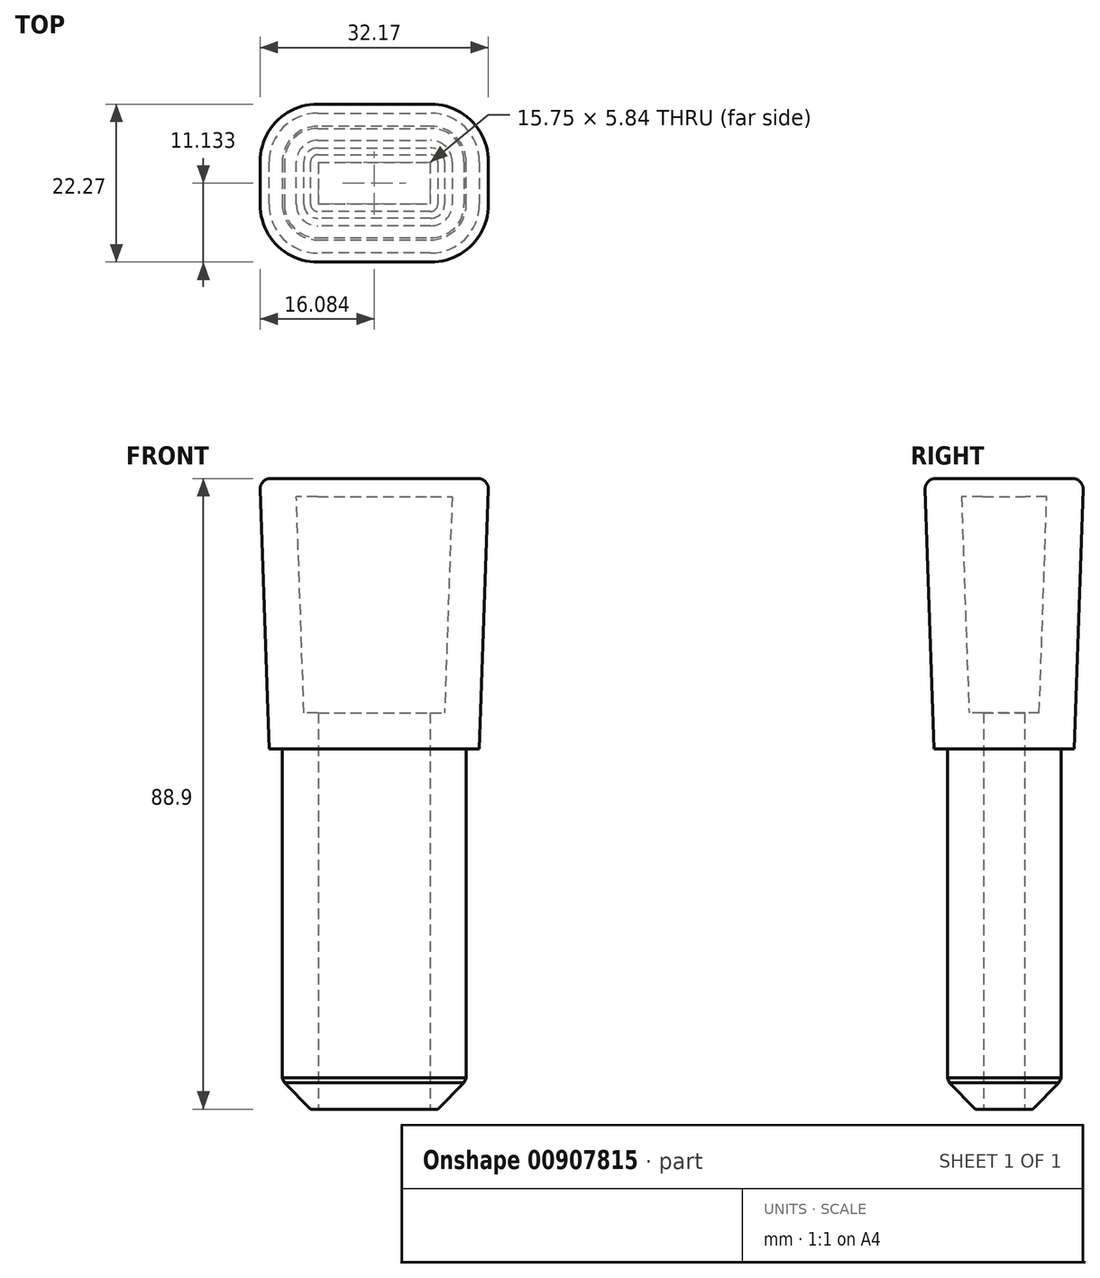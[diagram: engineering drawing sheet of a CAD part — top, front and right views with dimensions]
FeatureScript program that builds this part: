
annotation { "Feature Type Name" : "Feature", "Feature Type Description" : "" }
export const myFeature = defineFeature(function(context is Context, id is Id, definition is map)
    precondition{}
    {
        {
            var Q0;
            Q0=qCreatedBy(makeId("Top.planeOp"),FACE);
            var sketch = newSketch(context, id + "F0", { "sketchPlane" : qUnion([Q0])});
            skLineSegment(sketch, "E0.bottom", {"start": v(5, 0.5) * mm, "end": v(20.9, 0.5) * mm});
            skLineSegment(sketch, "E0.top", {"start": v(5, -15.5) * mm, "end": v(20.9, -15.5) * mm});
            skLineSegment(sketch, "E0.left", {"start": v(0, -4.5) * mm, "end": v(0, -10.5) * mm});
            skLineSegment(sketch, "E0.right", {"start": v(25.9, -4.5) * mm, "end": v(25.9, -10.5) * mm});
            skPoint(sketch, "E1.visualSharp", {"position": v(0, 0.5) * mm});
            skArc(sketch, "E1.filletArc", {"start": v(5, 0.5) * mm, "mid": v(1.46, -0.97) * mm, "end": v(0, -4.5) * mm});
            skPoint(sketch, "E2.visualSharp", {"position": v(25.9, 0.5) * mm});
            skArc(sketch, "E2.filletArc", {"start": v(25.9, -4.5) * mm, "mid": v(24.44, -0.97) * mm, "end": v(20.9, 0.5) * mm});
            skPoint(sketch, "E3.visualSharp", {"position": v(25.9, -15.5) * mm});
            skArc(sketch, "E3.filletArc", {"start": v(20.9, -15.5) * mm, "mid": v(24.44, -14.04) * mm, "end": v(25.9, -10.5) * mm});
            skPoint(sketch, "E4.visualSharp", {"position": v(0, -15.5) * mm});
            skArc(sketch, "E4.filletArc", {"start": v(0, -10.5) * mm, "mid": v(1.46, -14.04) * mm, "end": v(5, -15.5) * mm});
            skSolve(sketch);
        }
        {
            var Q0;
            Q0=makeQuery(id+"F0.imprint","IMPRINT",FACE,{"disambiguationData":[TD([[makeQuery(id+"F0.imprint","IMPRINT",EDGE,{"derivedFrom":sQuery(id+"F0.wireOp",EDGE,"E0.bottom")}),-1.0]])]});
            extrude(context, id + "F1", {"entities" : qUnion([Q0]), "depth" : 50.8 * mm, "offsetDistance" : 25 * mm});
        }
        {
            var Q0;
            Q0=makeQuery(id+"F1.opExtrude","CAP_FACE",FACE,{"disambiguationData":[OSD([sQuery(id+"F0.wireOp",EDGE,"E0.bottom"),sQuery(id+"F0.wireOp",EDGE,"E0.top"),sQuery(id+"F0.wireOp",EDGE,"E0.left"),sQuery(id+"F0.wireOp",EDGE,"E0.right"),sQuery(id+"F0.wireOp",EDGE,"E1.filletArc"),sQuery(id+"F0.wireOp",EDGE,"E2.filletArc"),sQuery(id+"F0.wireOp",EDGE,"E3.filletArc"),sQuery(id+"F0.wireOp",EDGE,"E4.filletArc")])],"isStart":false});
            var sketch = newSketch(context, id + "F2", { "sketchPlane" : qUnion([Q0])});
            skArc(sketch, "E5.0", {"start": v(5, 2.35) * mm, "mid": v(0.15, 0.34) * mm, "end": v(-1.85, -4.5) * mm});
            skLineSegment(sketch, "E5.1", {"start": v(-1.85, -4.5) * mm, "end": v(-1.85, -10.5) * mm});
            skLineSegment(sketch, "E5.2", {"start": v(5, 2.35) * mm, "end": v(20.9, 2.35) * mm});
            skArc(sketch, "E5.3", {"start": v(-1.85, -10.5) * mm, "mid": v(0.15, -15.35) * mm, "end": v(5, -17.36) * mm});
            skArc(sketch, "E5.4", {"start": v(27.76, -4.5) * mm, "mid": v(25.75, 0.34) * mm, "end": v(20.9, 2.35) * mm});
            skLineSegment(sketch, "E5.5", {"start": v(27.76, -4.5) * mm, "end": v(27.76, -10.5) * mm});
            skArc(sketch, "E5.6", {"start": v(20.9, -17.36) * mm, "mid": v(25.75, -15.35) * mm, "end": v(27.76, -10.5) * mm});
            skLineSegment(sketch, "E5.7", {"start": v(5, -17.36) * mm, "end": v(20.9, -17.36) * mm});
            skSolve(sketch);
        }
        {
            var Q0;
            Q0 = qSketchRegion(id + "F2", true);
            extrude(context, id + "F3", {"entities" : qUnion([Q0]), "operationType" : NewBodyOperationType.ADD, "depth" : 38.1 * mm, "offsetDistance" : 25 * mm, "hasDraft" : true, "draftAngle" : 2 * degree});
        }
        {
            var Q0;
            Q0=makeQuery(id+"F3.opExtrude","CAP_FACE",FACE,{"disambiguationData":[OSD([sQuery(id+"F2.wireOp",EDGE,"E5.0"),sQuery(id+"F2.wireOp",EDGE,"E5.1"),sQuery(id+"F2.wireOp",EDGE,"E5.2"),sQuery(id+"F2.wireOp",EDGE,"E5.3"),sQuery(id+"F2.wireOp",EDGE,"E5.4"),sQuery(id+"F2.wireOp",EDGE,"E5.5"),sQuery(id+"F2.wireOp",EDGE,"E5.6"),sQuery(id+"F2.wireOp",EDGE,"E5.7")])],"isStart":false});
            var Q1;
            Q1=makeQuery(id+"F1.opExtrude","CAP_FACE",FACE,{"disambiguationData":[OSD([sQuery(id+"F0.wireOp",EDGE,"E0.bottom"),sQuery(id+"F0.wireOp",EDGE,"E0.top"),sQuery(id+"F0.wireOp",EDGE,"E0.left"),sQuery(id+"F0.wireOp",EDGE,"E0.right"),sQuery(id+"F0.wireOp",EDGE,"E1.filletArc"),sQuery(id+"F0.wireOp",EDGE,"E2.filletArc"),sQuery(id+"F0.wireOp",EDGE,"E3.filletArc"),sQuery(id+"F0.wireOp",EDGE,"E4.filletArc")])],"isStart":true});
            shell(context, id + "F4", {"entities" : qUnion([Q0, Q1]), "thickness" : 5.08 * mm});
        }
        {
            var Q0;
            Q0=makeQuery(id+"F1.opExtrude","CAP_EDGE",EDGE,{"disambiguationData":[OSD([sQuery(id+"F0.wireOp",EDGE,"E0.top")])],"isStart":true});
            chamfer(context, id + "F5", {"entities" : qUnion([Q0]), "width" : 4 * mm, "tangentPropagation" : true});
        }
        {
            var Q0;
            {var subQ0=sQuery(id+"F0.wireOp",EDGE,"E0.left");Q0=makeQuery(id+"F5.opChamfer","BLEND_EDGE",EDGE,{"blendedFrom":[makeQuery(id+"F1.opExtrude","CAP_EDGE",EDGE,{"disambiguationData":[OSD([subQ0])],"isStart":true}),makeQuery(id+"F1.opExtrude","SWEPT_FACE",FACE,{"disambiguationData":[OSD([subQ0])]})],"blendedInto":[makeQuery(id+"F1.opExtrude","SWEPT_FACE",FACE,{"disambiguationData":[OSD([subQ0])]})]});}
            chamfer(context, id + "F6", {"entities" : qUnion([Q0]), "width" : 1 * mm, "tangentPropagation" : true});
        }
        {
            var Q0;
            Q0=makeQuery(id+"F3.opExtrude","CAP_FACE",FACE,{"disambiguationData":[OSD([sQuery(id+"F2.wireOp",EDGE,"E5.0"),sQuery(id+"F2.wireOp",EDGE,"E5.1"),sQuery(id+"F2.wireOp",EDGE,"E5.2"),sQuery(id+"F2.wireOp",EDGE,"E5.3"),sQuery(id+"F2.wireOp",EDGE,"E5.4"),sQuery(id+"F2.wireOp",EDGE,"E5.5"),sQuery(id+"F2.wireOp",EDGE,"E5.6"),sQuery(id+"F2.wireOp",EDGE,"E5.7")])],"isStart":false});
            var sketch = newSketch(context, id + "F7", { "sketchPlane" : qUnion([Q0])});
            skLineSegment(sketch, "E6.0", {"start": v(29.1, -4.5) * mm, "end": v(29.1, -10.5) * mm});
            skArc(sketch, "E6.1", {"start": v(29.1, -4.5) * mm, "mid": v(26.7, 1.28) * mm, "end": v(20.9, 3.68) * mm});
            skLineSegment(sketch, "E6.2", {"start": v(5, 3.68) * mm, "end": v(20.9, 3.68) * mm});
            skArc(sketch, "E6.3", {"start": v(5, 3.68) * mm, "mid": v(-0.79, 1.28) * mm, "end": v(-3.18, -4.5) * mm});
            skArc(sketch, "E7.0", {"start": v(20.9, -18.7) * mm, "mid": v(26.7, -16.3) * mm, "end": v(29.1, -10.5) * mm});
            skLineSegment(sketch, "E7.1", {"start": v(5, -18.7) * mm, "end": v(20.9, -18.7) * mm});
            skArc(sketch, "E7.2", {"start": v(-3.18, -10.5) * mm, "mid": v(-0.79, -16.3) * mm, "end": v(5, -18.7) * mm});
            skLineSegment(sketch, "E7.3", {"start": v(-3.18, -4.5) * mm, "end": v(-3.18, -10.5) * mm});
            skSolve(sketch);
        }
        {
            var Q0;
            Q0 = qSketchRegion(id + "F7", true);
            extrude(context, id + "F8", {"entities" : qUnion([Q0]), "operationType" : NewBodyOperationType.ADD, "oppositeDirection" : true, "depth" : 2.54 * mm, "offsetDistance" : 25 * mm, "hasDraft" : true, "draftAngle" : 3 * degree, "draftPullDirection" : true});
        }
        {
            var Q0;
            Q0=makeQuery(id+"F3.opExtrude","CAP_EDGE",EDGE,{"disambiguationData":[OSD([sQuery(id+"F2.wireOp",EDGE,"E5.7")])],"isStart":false});
            var Q1;
            Q1=makeQuery(id+"F3.opExtrude","CAP_EDGE",EDGE,{"disambiguationData":[OSD([sQuery(id+"F2.wireOp",EDGE,"E5.3")])],"isStart":false});
            var Q2;
            Q2=makeQuery(id+"F3.opExtrude","CAP_EDGE",EDGE,{"disambiguationData":[OSD([sQuery(id+"F2.wireOp",EDGE,"E5.6")])],"isStart":false});
            var Q3;
            Q3=makeQuery(id+"F3.opExtrude","CAP_EDGE",EDGE,{"disambiguationData":[OSD([sQuery(id+"F2.wireOp",EDGE,"E5.5")])],"isStart":false});
            var Q4;
            Q4=makeQuery(id+"F3.opExtrude","CAP_EDGE",EDGE,{"disambiguationData":[OSD([sQuery(id+"F2.wireOp",EDGE,"E5.4")])],"isStart":false});
            var Q5;
            Q5=makeQuery(id+"F3.opExtrude","CAP_EDGE",EDGE,{"disambiguationData":[OSD([sQuery(id+"F2.wireOp",EDGE,"E5.2")])],"isStart":false});
            var Q6;
            Q6=makeQuery(id+"F3.opExtrude","CAP_EDGE",EDGE,{"disambiguationData":[OSD([sQuery(id+"F2.wireOp",EDGE,"E5.0")])],"isStart":false});
            fillet(context, id + "F10", {"entities" : qUnion([Q0, Q1, Q2, Q3, Q4, Q5, Q6]), "radius" : 1.5 * mm, "tangentPropagation" : true, "allowEdgeOverflow" : false});
        }
    });
